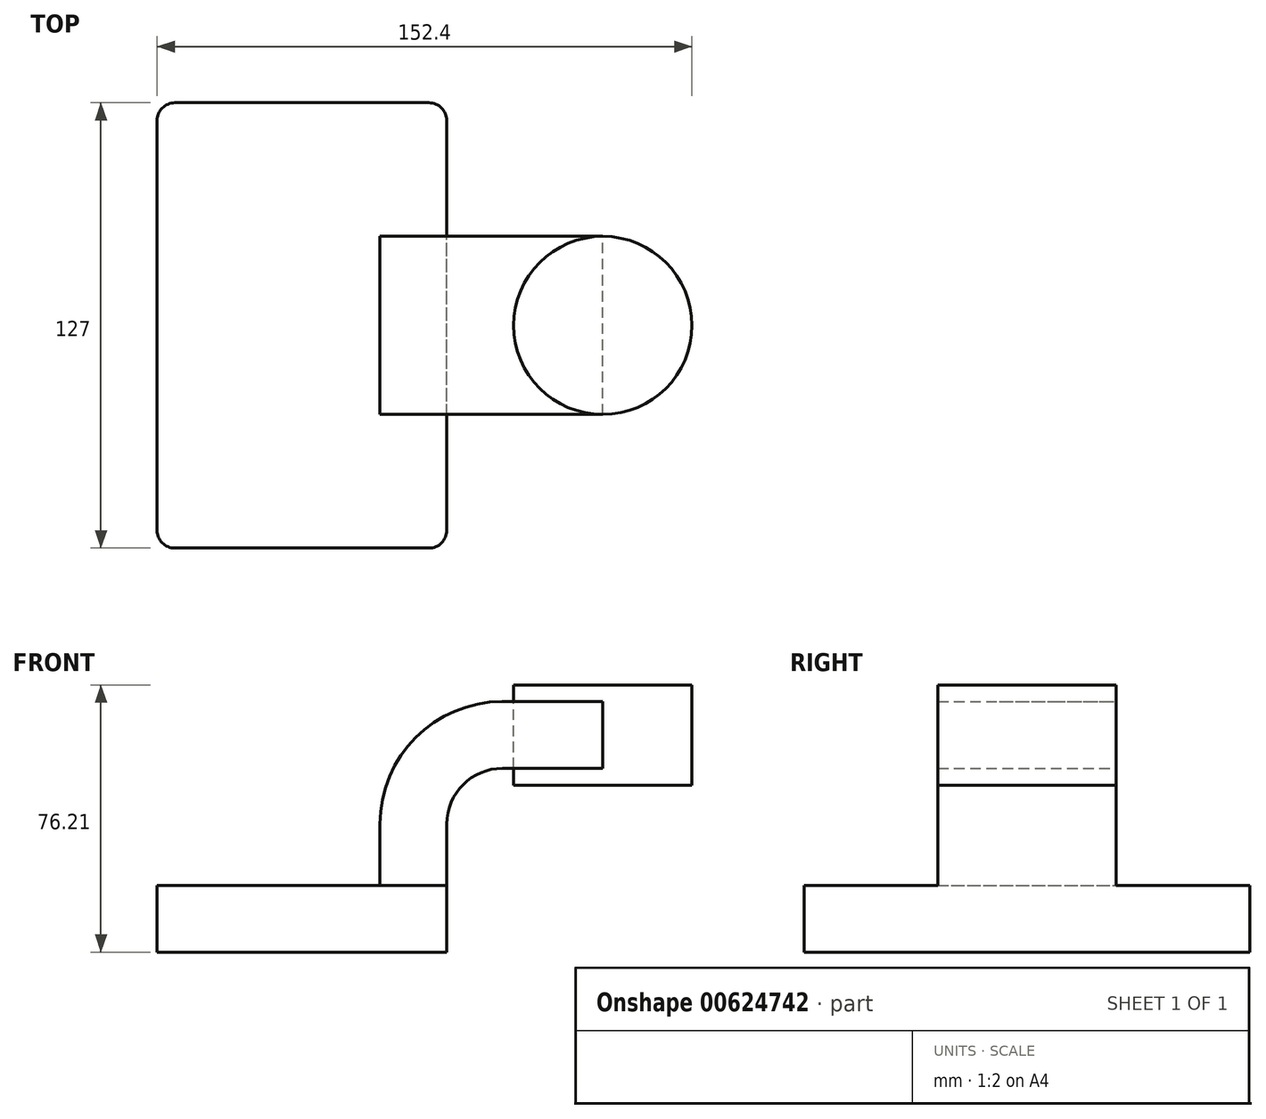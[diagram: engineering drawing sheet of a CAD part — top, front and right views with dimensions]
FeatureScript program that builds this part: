
annotation { "Feature Type Name" : "Feature", "Feature Type Description" : "" }
export const myFeature = defineFeature(function(context is Context, id is Id, definition is map)
    precondition{}
    {
        {
            var Q0;
            Q0=qCreatedBy(makeId("Front.planeOp"),FACE);
            var sketch = newSketch(context, id + "F0", { "sketchPlane" : qUnion([Q0])});
            skLineSegment(sketch, "E0.bottom", {"start": v(-41.28, -9.53) * mm, "end": v(41.28, -9.53) * mm});
            skLineSegment(sketch, "E0.top", {"start": v(-41.28, 9.53) * mm, "end": v(41.28, 9.53) * mm});
            skLineSegment(sketch, "E0.left", {"start": v(-41.28, -9.53) * mm, "end": v(-41.28, 9.53) * mm});
            skLineSegment(sketch, "E0.right", {"start": v(41.28, -9.53) * mm, "end": v(41.28, 9.52) * mm});
            skPoint(sketch, "E0.middle", {"position": v(0, 0) * mm});
            skLineSegment(sketch, "E1.bottom", {"start": v(60.32, 66.67) * mm, "end": v(111.12, 66.67) * mm});
            skLineSegment(sketch, "E1.top", {"start": v(60.32, 38.1) * mm, "end": v(111.12, 38.1) * mm});
            skLineSegment(sketch, "E1.left", {"start": v(60.32, 66.67) * mm, "end": v(60.32, 38.1) * mm});
            skLineSegment(sketch, "E1.right", {"start": v(111.12, 66.67) * mm, "end": v(111.12, 38.1) * mm});
            skPoint(sketch, "E1.middle", {"position": v(85.72, 52.39) * mm});
            skLineSegment(sketch, "E2", {"start": v(41.28, 9.52) * mm, "end": v(41.28, 27) * mm});
            skArc(sketch, "E3", {"start": v(41.27, 27) * mm, "mid": v(45.92, 38.23) * mm, "end": v(57.15, 42.88) * mm});
            skLineSegment(sketch, "E4", {"start": v(57.15, 42.88) * mm, "end": v(85.72, 42.88) * mm});
            skLineSegment(sketch, "E5.0", {"start": v(57.15, 61.93) * mm, "end": v(85.72, 61.93) * mm});
            skArc(sketch, "E5.1", {"start": v(22.22, 27) * mm, "mid": v(32.45, 51.7) * mm, "end": v(57.15, 61.93) * mm});
            skLineSegment(sketch, "E5.2", {"start": v(22.22, 9.52) * mm, "end": v(22.22, 27) * mm});
            skLineSegment(sketch, "E6", {"start": v(85.72, 42.88) * mm, "end": v(85.72, 66.67) * mm});
            skFitSpline(sketch, "E7", {"points": [v(-41.28, 9.53) * mm, v(57.15, 61.93) * mm], "startDerivative": vector(2.76, 83.01) * mm, "endDerivative": vector(171.45, 0.22) * mm});
            skLineSegment(sketch, "E8", {"start": v(85.72, 66.67) * mm, "end": v(85.72, 38.1) * mm});
            skSolve(sketch);
        }
        {
            var Q0;
            Q0=makeQuery(id+"F0.imprint","IMPRINT",FACE,{"disambiguationData":[TD([[makeQuery(id+"F0.imprint","IMPRINT",EDGE,{"derivedFrom":sQuery(id+"F0.wireOp",EDGE,"E0.bottom")}),1.0]])]});
            extrude(context, id + "F1", {"entities" : qUnion([Q0]), "endBound" : BoundingType.SYMMETRIC, "depth" : 127 * mm, "offsetDistance" : 25.4 * mm});
        }
        {
            var Q0;
            {var subQ1=sQuery(id+"F0.wireOp",EDGE,"E2");Q0=makeQuery(id+"F0.imprint","IMPRINT",FACE,{"disambiguationData":[TD([[makeQuery(id+"F0.imprint","IMPRINT",EDGE,{"derivedFrom":subQ1}),1.0]])]});}
            var Q1;
            {var subQ0=sQuery(id+"F0.wireOp",EDGE,"E5.0");var subQ1=sQuery(id+"F0.wireOp",EDGE,"E1.left");var subQ2=makeQuery(id+"F0.imprint","INTERSECT",VERTEX,{"derivedFrom":[subQ1,subQ0]});Q1=makeQuery(id+"F0.imprint","IMPRINT",FACE,{"disambiguationData":[TD([[makeQuery(id+"F0.imprint","IMPRINT",EDGE,{"disambiguationData":[TD([[subQ2,-1.0]])],"derivedFrom":subQ1}),1.0]])]});}
            extrude(context, id + "F2", {"entities" : qUnion([Q0, Q1]), "operationType" : NewBodyOperationType.ADD, "endBound" : BoundingType.SYMMETRIC, "depth" : 50.8 * mm, "offsetDistance" : 25.4 * mm});
        }
        {
            var Q0;
            {var subQ4=sQuery(id+"F0.wireOp",EDGE,"E5.1");Q0=makeQuery(id+"F0.imprint","IMPRINT",FACE,{"disambiguationData":[TD([[makeQuery(id+"F0.imprint","IMPRINT",EDGE,{"derivedFrom":subQ4}),1.0]])]});}
            extrude(context, id + "F3", {"entities" : qUnion([Q0]), "operationType" : NewBodyOperationType.ADD, "endBound" : BoundingType.SYMMETRIC, "depth" : 15.88 * mm, "offsetDistance" : 25.4 * mm});
        }
        {
            var Q0;
            {var subQ0=sQuery(id+"F0.wireOp",EDGE,"E1.right");Q0=makeQuery(id+"F0.imprint","IMPRINT",FACE,{"disambiguationData":[TD([[makeQuery(id+"F0.imprint","IMPRINT",EDGE,{"derivedFrom":subQ0}),-1.0]])]});}
            var Q1;
            Q1=sQuery(id+"F0.wireOp",EDGE,"E8");
            revolve(context, id + "F4", {"entities" : qUnion([Q0]), "axis" : qUnion([Q1]), "revolveType" : RevolveType.FULL});
        }
        {
            var Q0;
            Q0=makeQuery(id+"F1.opExtrude","CAP_EDGE",EDGE,{"disambiguationData":[OSD([sQuery(id+"F0.wireOp",EDGE,"E0.left")])],"isStart":false});
            var Q1;
            Q1=makeQuery(id+"F1.opExtrude","CAP_EDGE",EDGE,{"disambiguationData":[OSD([sQuery(id+"F0.wireOp",EDGE,"E0.right")])],"isStart":false});
            var Q2;
            Q2=makeQuery(id+"F1.opExtrude","CAP_EDGE",EDGE,{"disambiguationData":[OSD([sQuery(id+"F0.wireOp",EDGE,"E0.right")])],"isStart":true});
            var Q3;
            Q3=makeQuery(id+"F1.opExtrude","CAP_EDGE",EDGE,{"disambiguationData":[OSD([sQuery(id+"F0.wireOp",EDGE,"E0.left")])],"isStart":true});
            fillet(context, id + "F5", {"entities" : qUnion([Q0, Q1, Q2, Q3]), "radius" : 5.08 * mm, "tangentPropagation" : true, "allowEdgeOverflow" : false});
        }
    });
